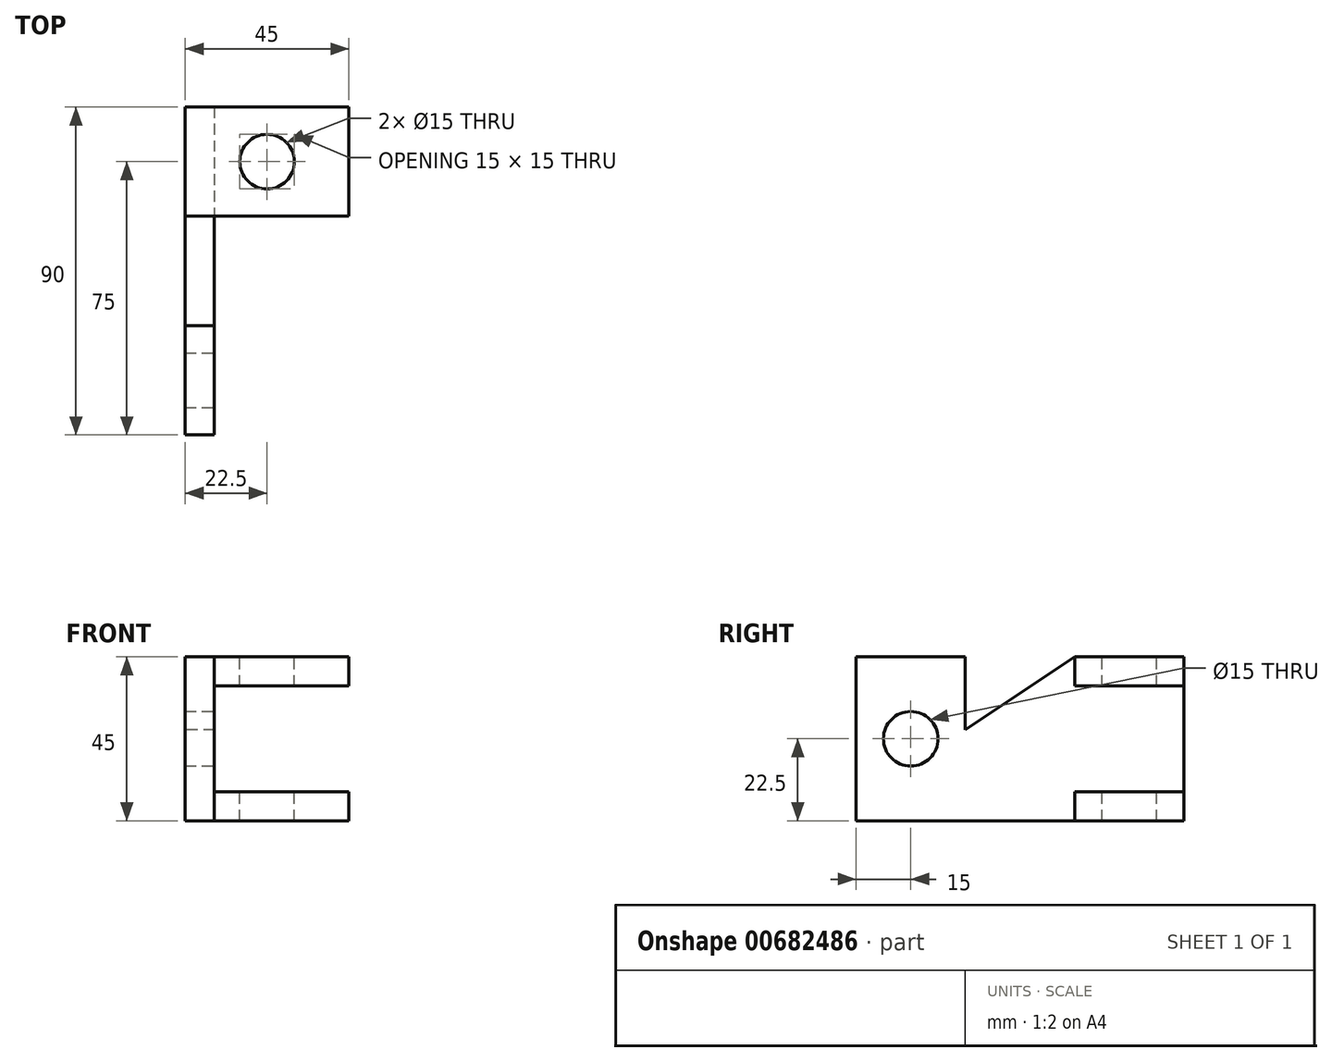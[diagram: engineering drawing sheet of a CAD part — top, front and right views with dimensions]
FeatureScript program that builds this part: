
annotation { "Feature Type Name" : "Feature", "Feature Type Description" : "" }
export const myFeature = defineFeature(function(context is Context, id is Id, definition is map)
    precondition{}
    {
        {
            var Q0;
            Q0=qCreatedBy(makeId("Right.planeOp"),FACE);
            var sketch = newSketch(context, id + "F0", { "sketchPlane" : qUnion([Q0])});
            skLineSegment(sketch, "E0", {"start": v(-90, 45) * mm, "end": v(-90, 0) * mm});
            skLineSegment(sketch, "E1", {"start": v(-90, 0) * mm, "end": v(0, 0) * mm});
            skLineSegment(sketch, "E2", {"start": v(0, 0) * mm, "end": v(0, 45) * mm});
            skLineSegment(sketch, "E3", {"start": v(-90, 45) * mm, "end": v(-60, 45) * mm});
            skLineSegment(sketch, "E4", {"start": v(0, 45) * mm, "end": v(-30, 45) * mm});
            skLineSegment(sketch, "E5", {"start": v(-60, 45) * mm, "end": v(-60, 25) * mm});
            skLineSegment(sketch, "E6", {"start": v(-60, 25) * mm, "end": v(-30, 45) * mm});
            skSolve(sketch);
        }
        {
            var Q0;
            Q0=makeQuery(id+"F0.imprint","IMPRINT",FACE,{"disambiguationData":[TD([[makeQuery(id+"F0.imprint","IMPRINT",EDGE,{"derivedFrom":sQuery(id+"F0.wireOp",EDGE,"E0")}),1.0]])]});
            extrude(context, id + "F1", {"entities" : qUnion([Q0]), "depth" : 8 * mm, "offsetDistance" : 25 * mm});
        }
        {
            var Q0;
            Q0=makeQuery(id+"F1.opExtrude","CAP_FACE",FACE,{"disambiguationData":[OSD([sQuery(id+"F0.wireOp",EDGE,"E0"),sQuery(id+"F0.wireOp",EDGE,"E1"),sQuery(id+"F0.wireOp",EDGE,"E2"),sQuery(id+"F0.wireOp",EDGE,"E3"),sQuery(id+"F0.wireOp",EDGE,"E4"),sQuery(id+"F0.wireOp",EDGE,"E5"),sQuery(id+"F0.wireOp",EDGE,"E6")])],"isStart":false});
            var sketch = newSketch(context, id + "F2", { "sketchPlane" : qUnion([Q0])});
            skLineSegment(sketch, "E7.bottom", {"start": v(0, 0) * mm, "end": v(-30, 0) * mm});
            skLineSegment(sketch, "E7.top", {"start": v(0, 8) * mm, "end": v(-30, 8) * mm});
            skLineSegment(sketch, "E7.left", {"start": v(0, 0) * mm, "end": v(0, 8) * mm});
            skLineSegment(sketch, "E7.right", {"start": v(-30, 0) * mm, "end": v(-30, 8) * mm});
            skLineSegment(sketch, "E8.bottom", {"start": v(0, 45) * mm, "end": v(-30, 45) * mm});
            skLineSegment(sketch, "E8.top", {"start": v(0, 37) * mm, "end": v(-30, 37) * mm});
            skLineSegment(sketch, "E8.left", {"start": v(0, 45) * mm, "end": v(0, 37) * mm});
            skLineSegment(sketch, "E8.right", {"start": v(-30, 45) * mm, "end": v(-30, 37) * mm});
            skPoint(sketch, "E9", {"position": v(-75, 22.5) * mm});
            skSolve(sketch);
        }
        {
            var Q0;
            Q0=makeQuery(id+"F2.imprint","IMPRINT",FACE,{"disambiguationData":[TD([[makeQuery(id+"F2.imprint","IMPRINT",EDGE,{"derivedFrom":sQuery(id+"F2.wireOp",EDGE,"E7.bottom")}),1.0]])]});
            var Q1;
            Q1=makeQuery(id+"F2.imprint","IMPRINT",FACE,{"disambiguationData":[TD([[makeQuery(id+"F2.imprint","IMPRINT",EDGE,{"derivedFrom":sQuery(id+"F2.wireOp",EDGE,"E8.bottom")}),1.0]])]});
            extrude(context, id + "F3", {"entities" : qUnion([Q0, Q1]), "operationType" : NewBodyOperationType.ADD, "depth" : 37 * mm, "offsetDistance" : 25 * mm});
        }
        {
            var Q0;
            Q0=makeQuery(id+"F3.boolean.opBoolean","MERGE",FACE,{"derivedFrom":[makeQuery(id+"F1.opExtrude","SWEPT_FACE",FACE,{"disambiguationData":[OSD([sQuery(id+"F0.wireOp",EDGE,"E4")])]}),makeQuery(id+"F3.opExtrude","SWEPT_FACE",FACE,{"disambiguationData":[OSD([sQuery(id+"F2.wireOp",EDGE,"E8.bottom")])]})]});
            var sketch = newSketch(context, id + "F4", { "sketchPlane" : qUnion([Q0])});
            skSolve(sketch);
        }
        {
            var Q0;
            {var subQ2=sQuery(id+"F0.wireOp",EDGE,"E4");Q0=makeQuery(id+"F4.imprint","IMPRINT",FACE,{"disambiguationData":[TD([[makeQuery(id+"F4.imprint","IMPRINT",EDGE,{"derivedFrom":makeQuery(id+"F1.opExtrude","CAP_EDGE",EDGE,{"disambiguationData":[OSD([subQ2])],"isStart":true})}),1.0]])]});}
            var sketch = newSketch(context, id + "F5", { "sketchPlane" : qUnion([Q0])});
            skPoint(sketch, "E10", {"position": v(22.5, -15) * mm});
            skSolve(sketch);
        }
        {
            var Q0;
            Q0=sQuery(id+"F5.wireOp",VERTEX,"E10");
            var Q1;
            Q1=makeQuery(id+"F1.opExtrude","SWEPT_BODY",BODY,{"disambiguationData":[OSD([sQuery(id+"F0.wireOp",EDGE,"E0"),sQuery(id+"F0.wireOp",EDGE,"E1"),sQuery(id+"F0.wireOp",EDGE,"E2"),sQuery(id+"F0.wireOp",EDGE,"E3"),sQuery(id+"F0.wireOp",EDGE,"E4"),sQuery(id+"F0.wireOp",EDGE,"E5"),sQuery(id+"F0.wireOp",EDGE,"E6")])]});
            hole(context, id + "F6", {"style" : HoleStyle.SIMPLE, "endStyle" : HoleEndStyle.THROUGH, "holeDiameter" : 15 * mm, "majorDiameter" : 5 * mm, "isTappedThrough" : true, "tappedDepth" : 12 * mm, "tapClearance" : 3, "locations" : qUnion([Q0]), "scope" : qUnion([Q1])});
        }
        {
            var Q0;
            Q0=sQuery(id+"F2.wireOp",VERTEX,"E9");
            var Q1;
            Q1=makeQuery(id+"F1.opExtrude","SWEPT_BODY",BODY,{"disambiguationData":[OSD([sQuery(id+"F0.wireOp",EDGE,"E0"),sQuery(id+"F0.wireOp",EDGE,"E1"),sQuery(id+"F0.wireOp",EDGE,"E2"),sQuery(id+"F0.wireOp",EDGE,"E3"),sQuery(id+"F0.wireOp",EDGE,"E4"),sQuery(id+"F0.wireOp",EDGE,"E5"),sQuery(id+"F0.wireOp",EDGE,"E6")])]});
            hole(context, id + "F7", {"style" : HoleStyle.SIMPLE, "endStyle" : HoleEndStyle.BLIND, "holeDiameter" : 15 * mm, "majorDiameter" : 5 * mm, "holeDepth" : 8 * mm, "isTappedThrough" : true, "tappedDepth" : 12 * mm, "tapClearance" : 3, "locations" : qUnion([Q0]), "scope" : qUnion([Q1])});
        }
    });
